# Revit family: Building-IEC309Connections-GEWISS-67IB-INTERLOCKED-SOCKET-OUTLETS_IP67_WITH_BOTTOM_63A
name_source: partatom
category: Apparecchi elettrici
units: mm (PartAtom-declared; Revit-internal decimal feet)

## family parameters
Condiviso = Sì
Host = Superficie
Mantenere orientamento annotazione = Sì
Punto di calcolo locali = Sì
Quota connettore circolare = Usa diametro
Taglio con vuoti quando caricato = Sì
Tipo di parte = Normale

## types (11) — shared parameters
Catalogue = BUILDING
Catalogue Range = 67 IB
Corpo presa = GEWISS -BLU
Electrocod = 2222
Frequency = 50/60 Hz
Glow Wire Test = 850 °C (IB socket) - 650 °C (bottom)
Glow wire test: = 850 °C (IB socket) - 650 °C (bottom)
IDF = 51023168-ce68-4f6c-bb69-d728f941b970
IDT = a25d3694-d0a1-482b-9cd4-b67b9b60fa6b
IP degree = IP67
Immagine tipo = F.jpg
Operating temperature: = -25 +40 °C
Produttore = GEWISS S.p.A.
Prospetto di default = 1219 mm
Protection = NO (SBF)
Rated current (A) = 63
Rated current (In) = 63
Rated frequency (Hz) = 50/60 Hz
SEO = Socket outlet
Shock resistance = IK08
Simbolo presa = PRESAINDSTAGNA : 3P
Struttura = Grigio RAL - 7035
Technical sheet = https://www.gewiss.com
Thermo-pressure with ball = 125 °C (IB socket) - 80 °C (bottom)
Typology = Vertical
URL = https://www.gewiss.com
Version file RFA = 21.4
With back-mounting box = Yes
Working temperature = -25 ÷ +40 °C
presa = Giallo
zero-valued in all types: giallo

## per-type parameters (varying)
| type | Colour | Colour: | Descrizione | EAN code | Modello | No. of poles | Number of poles | Rated voltage | Rated voltage: | Reference h |
| GW67266N - 63A 3P+N+E 500V V.INT.SOCK.O.W.B.7H SBF | Black | Black | 63A 3P+N+E 500V V.INT.SOCK.O.W.B.7H SBF | 8011564742369 | GW67266N | 3P+N+E | 3P+N+E | 480 - 500 V | 480 - 500 V | 7 |
| GW67265N - 63A 3P+E 500V V.INT.SOCK.O.W.B.7H SBF | Black | Black | 63A 3P+E 500V V.INT.SOCK.O.W.B.7H SBF | 8011564742352 | GW67265N | 3P+E | 3P+E | 480 - 500 V | 480 - 500 V | 7 |
| GW67260N - 63A 3P+E 230V V.INT.SOCK.O.W.B.9H SBF | Blue | Blue | 63A 3P+E 230V V.INT.SOCK.O.W.B.9H SBF | 8011564742307 | GW67260N | 3P+E | 3P+E | 200 - 250 V | 200 - 250 V | 9 |
| GW67258N - 63A 3P+N+E 110V V.INT.SOCK.O.W.B.4H SBF | Yellow | Yellow | 63A 3P+N+E 110V V.INT.SOCK.O.W.B.4H SBF | 8011564742284 | GW67258N | 3P+N+E | 3P+N+E | 100 - 130 V | 100 - 130 V | 4 |
| GW67262N - 63A 2P+E 400V V.INT.SOCK.O.W.B.9H SBF | Red | Red | 63A 2P+E 400V V.INT.SOCK.O.W.B.9H SBF | 8011564742321 | GW67262N | 2P+E | 2P+E | 380 - 415 V | 380 - 415 V | 9 |
| GW67259N - 63A 2P+E 230V V.INT.SOCK.O.W.B.6H SBF | Blue | Blue | 63A 2P+E 230V V.INT.SOCK.O.W.B.6H SBF | 8011564742291 | GW67259N | 2P+E | 2P+E | 200 - 250 V | 200 - 250 V | 6 |
| GW67261N - 63A 3P+N+E 230V V.INT.SOCK.O.W.B.9H SBF | Blue | Blue | 63A 3P+N+E 230V V.INT.SOCK.O.W.B.9H SBF | 8011564742314 | GW67261N | 3P+N+E | 3P+N+E | 200 - 250 V | 200 - 250 V | 9 |
| GW67264N - 63A 3P+N+E 400V V.INT.SOCK.O.W.B.6H SBF | Red | Red | 63A 3P+N+E 400V V.INT.SOCK.O.W.B.6H SBF | 8011564742345 | GW67264N | 3P+N+E | 3P+N+E | 380 - 415 V | 380 - 415 V | 6 |
| GW67257N - 63A 3P+E 110V V.INT.SOCK.O.W.B.4H SBF | Yellow | Yellow | 63A 3P+E 110V V.INT.SOCK.O.W.B.4H SBF | 8011564742277 | GW67257N | 3P+E | 3P+E | 100 - 130 V | 100 - 130 V | 4 |
| GW67263N - 63A 3P+E 400V V.INT.SOCK.O.W.B.6H SBF | Red | Red | 63A 3P+E 400V V.INT.SOCK.O.W.B.6H SBF | 8011564742338 | GW67263N | 3P+E | 3P+E | 380 - 415 V | 380 - 415 V | 6 |
| GW67256N - 63A 2P+E 110V V.INT.SOCK.O.W.B.4H SBF | Yellow | Yellow | 63A 2P+E 110V V.INT.SOCK.O.W.B.4H SBF | 8011564742260 | GW67256N | 2P+E | 2P+E | 100 - 130 V | 100 - 130 V | 4 |

## geometry (parser evidence)
native form markers: Sweep x4
no freeform markers — native parametric forms only
